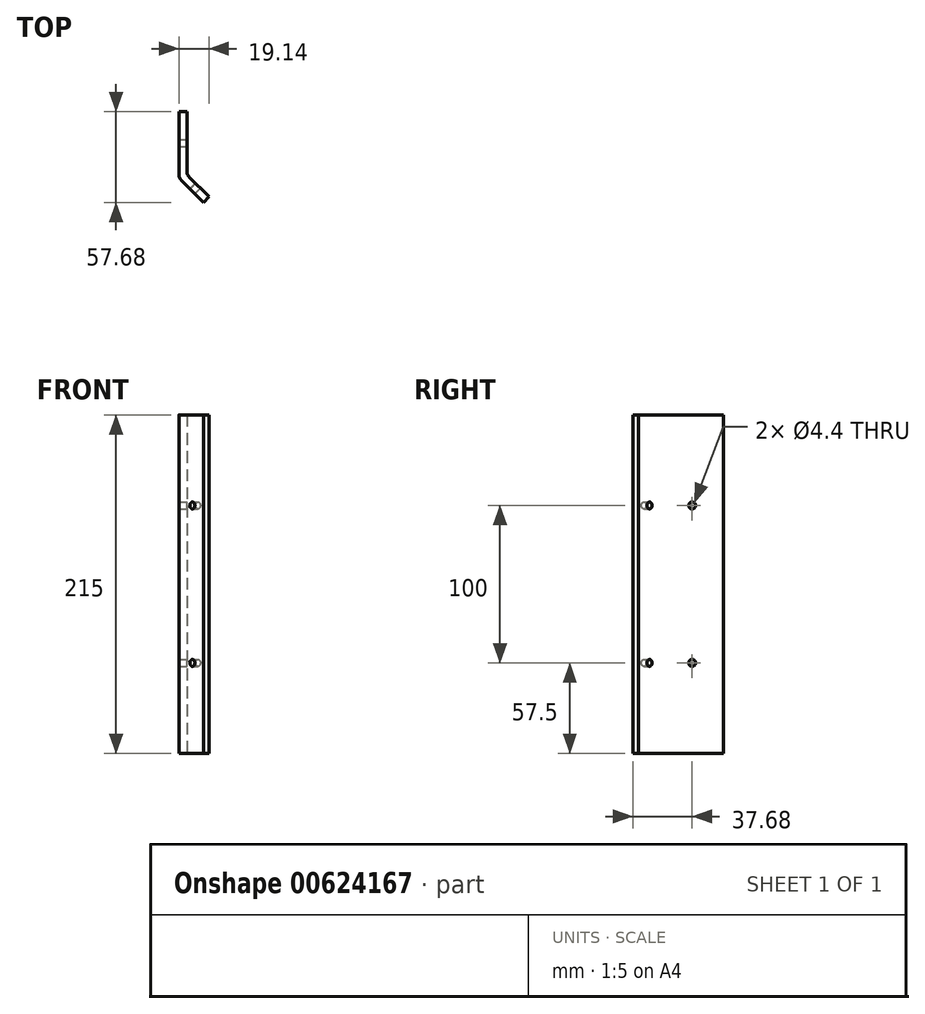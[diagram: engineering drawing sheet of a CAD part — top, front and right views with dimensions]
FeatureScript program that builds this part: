
annotation { "Feature Type Name" : "Feature", "Feature Type Description" : "" }
export const myFeature = defineFeature(function(context is Context, id is Id, definition is map)
    precondition{}
    {
        {
            var Q0;
            Q0=qCreatedBy(makeId("Top.planeOp"),FACE);
            var sketch = newSketch(context, id + "F0", { "sketchPlane" : qUnion([Q0])});
            skLineSegment(sketch, "E0.bottom", {"start": v(0, 40) * mm, "end": v(-5, 40) * mm});
            skLineSegment(sketch, "E0.top", {"start": v(0, 0) * mm, "end": v(-5, 0) * mm});
            skLineSegment(sketch, "E0.left", {"start": v(0, 40) * mm, "end": v(0, 2.07) * mm});
            skLineSegment(sketch, "E0.right", {"start": v(-5, 40) * mm, "end": v(-5, 0) * mm});
            skLineSegment(sketch, "E1", {"start": v(1.46, -1.46) * mm, "end": v(14.14, -14.14) * mm});
            skLineSegment(sketch, "E2", {"start": v(14.14, -14.14) * mm, "end": v(10.6, -17.68) * mm});
            skLineSegment(sketch, "E3", {"start": v(10.6, -17.68) * mm, "end": v(-3.54, -3.54) * mm});
            skArc(sketch, "E4", {"start": v(-5, 0) * mm, "mid": v(-4.62, -1.91) * mm, "end": v(-3.54, -3.54) * mm});
            skArc(sketch, "E5.filletArc", {"start": v(0, 2.07) * mm, "mid": v(0.38, 0.16) * mm, "end": v(1.46, -1.46) * mm});
            skSolve(sketch);
        }
        {
            var Q0;
            Q0=makeQuery(id+"F0.imprint","IMPRINT",FACE,{"disambiguationData":[TD([[makeQuery(id+"F0.imprint","IMPRINT",EDGE,{"derivedFrom":sQuery(id+"F0.wireOp",EDGE,"E0.bottom")}),1.0]])]});
            extrude(context, id + "F1", {"entities" : qUnion([Q0]), "depth" : 215 * mm, "offsetDistance" : 25 * mm});
        }
        {
            var Q0;
            Q0=makeQuery(id+"F1.opExtrude","SWEPT_FACE",FACE,{"disambiguationData":[OSD([sQuery(id+"F0.wireOp",EDGE,"E0.left")])]});
            var sketch = newSketch(context, id + "F2", { "sketchPlane" : qUnion([Q0])});
            skPoint(sketch, "E6", {"position": v(20, 157.5) * mm});
            skPoint(sketch, "E7", {"position": v(20, 57.5) * mm});
            skSolve(sketch);
        }
        {
            var Q0;
            Q0=sQuery(id+"F2.wireOp",VERTEX,"E6");
            var Q1;
            Q1=sQuery(id+"F2.wireOp",VERTEX,"E7");
            var Q2;
            Q2=makeQuery(id+"F1.opExtrude","SWEPT_BODY",BODY,{"disambiguationData":[OSD([sQuery(id+"F0.wireOp",EDGE,"E0.bottom"),sQuery(id+"F0.wireOp",EDGE,"E0.left"),sQuery(id+"F0.wireOp",EDGE,"E0.right"),sQuery(id+"F0.wireOp",EDGE,"E1"),sQuery(id+"F0.wireOp",EDGE,"E2"),sQuery(id+"F0.wireOp",EDGE,"E3"),sQuery(id+"F0.wireOp",EDGE,"E4"),sQuery(id+"F0.wireOp",EDGE,"E5.filletArc")])]});
            hole(context, id + "F3", {"style" : HoleStyle.SIMPLE, "endStyle" : HoleEndStyle.THROUGH, "standardTappedOrClearance" : lookupTablePath({ "standard" : "ISO", "fit" : "Normal", "size" : "M4", "type" : "Clearance" }), "standardBlindInLast" : lookupTablePath({ "fit" : "Standard", "standard" : "ISO", "size" : "M4", "type" : "Clearance" }), "holeDiameter" : 4.4 * mm, "majorDiameter" : 5 * mm, "isTappedThrough" : true, "tappedDepth" : 12 * mm, "tapClearance" : 3, "locations" : qUnion([Q0, Q1]), "scope" : qUnion([Q2])});
        }
        {
            var Q0;
            Q0=makeQuery(id+"F1.opExtrude","SWEPT_FACE",FACE,{"disambiguationData":[OSD([sQuery(id+"F0.wireOp",EDGE,"E1")])]});
            var sketch = newSketch(context, id + "F4", { "sketchPlane" : qUnion([Q0])});
            skPoint(sketch, "E8", {"position": v(-10, 157.5) * mm});
            skPoint(sketch, "E9", {"position": v(-10, 57.5) * mm});
            skSolve(sketch);
        }
        {
            var Q0;
            Q0=sQuery(id+"F4.wireOp",VERTEX,"E8");
            var Q1;
            Q1=sQuery(id+"F4.wireOp",VERTEX,"E9");
            var Q2;
            Q2=makeQuery(id+"F1.opExtrude","SWEPT_BODY",BODY,{"disambiguationData":[OSD([sQuery(id+"F0.wireOp",EDGE,"E0.bottom"),sQuery(id+"F0.wireOp",EDGE,"E0.left"),sQuery(id+"F0.wireOp",EDGE,"E0.right"),sQuery(id+"F0.wireOp",EDGE,"E1"),sQuery(id+"F0.wireOp",EDGE,"E2"),sQuery(id+"F0.wireOp",EDGE,"E3"),sQuery(id+"F0.wireOp",EDGE,"E4"),sQuery(id+"F0.wireOp",EDGE,"E5.filletArc")])]});
            hole(context, id + "F5", {"style" : HoleStyle.SIMPLE, "endStyle" : HoleEndStyle.THROUGH, "standardTappedOrClearance" : lookupTablePath({ "standard" : "ISO", "fit" : "Normal", "size" : "M4", "type" : "Clearance" }), "standardBlindInLast" : lookupTablePath({ "fit" : "Standard", "standard" : "ISO", "size" : "M4", "type" : "Clearance" }), "holeDiameter" : 4.4 * mm, "majorDiameter" : 5 * mm, "isTappedThrough" : true, "tappedDepth" : 12 * mm, "tapClearance" : 3, "locations" : qUnion([Q0, Q1]), "scope" : qUnion([Q2])});
        }
    });
